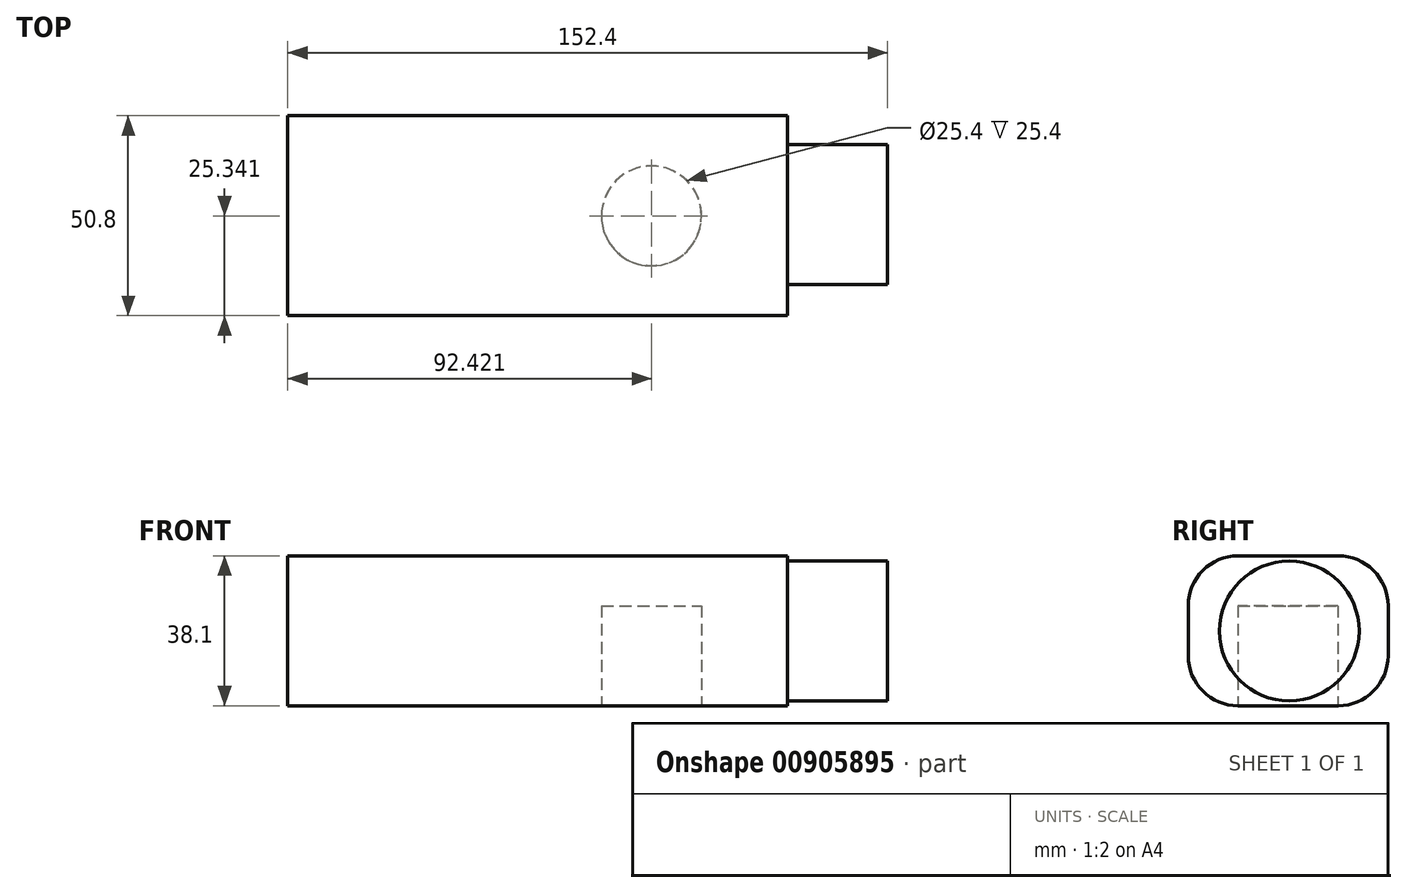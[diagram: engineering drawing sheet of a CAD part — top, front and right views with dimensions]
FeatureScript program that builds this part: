
annotation { "Feature Type Name" : "Feature", "Feature Type Description" : "" }
export const myFeature = defineFeature(function(context is Context, id is Id, definition is map)
    precondition{}
    {
        {
            var Q0;
            Q0=qCreatedBy(makeId("Right.planeOp"),FACE);
            var sketch = newSketch(context, id + "F0", { "sketchPlane" : qUnion([Q0])});
            skLineSegment(sketch, "E0.bottom", {"start": v(-48.2, 38.36) * mm, "end": v(2.6, 38.36) * mm});
            skLineSegment(sketch, "E0.top", {"start": v(-48.2, 0.26) * mm, "end": v(2.6, 0.26) * mm});
            skLineSegment(sketch, "E0.left", {"start": v(-48.2, 38.36) * mm, "end": v(-48.2, 0.26) * mm});
            skLineSegment(sketch, "E0.right", {"start": v(2.6, 38.36) * mm, "end": v(2.6, 0.26) * mm});
            skSolve(sketch);
        }
        {
            var Q0;
            Q0 = qSketchRegion(id + "F0", true);
            extrude(context, id + "F1", {"entities" : qUnion([Q0]), "depth" : 127 * mm, "offsetDistance" : 25.4 * mm});
        }
        {
            var Q0;
            Q0=makeQuery(id+"F1.opExtrude","SWEPT_EDGE",EDGE,{"disambiguationData":[OSD([sQuery(id+"F0.wireOp",EDGE,"E0.bottom"),sQuery(id+"F0.wireOp",EDGE,"E0.left")])]});
            var Q1;
            Q1=makeQuery(id+"F1.opExtrude","SWEPT_EDGE",EDGE,{"disambiguationData":[OSD([sQuery(id+"F0.wireOp",EDGE,"E0.bottom"),sQuery(id+"F0.wireOp",EDGE,"E0.right")])]});
            var Q2;
            Q2=makeQuery(id+"F1.opExtrude","SWEPT_EDGE",EDGE,{"disambiguationData":[OSD([sQuery(id+"F0.wireOp",EDGE,"E0.top"),sQuery(id+"F0.wireOp",EDGE,"E0.left")])]});
            var Q3;
            Q3=makeQuery(id+"F1.opExtrude","SWEPT_EDGE",EDGE,{"disambiguationData":[OSD([sQuery(id+"F0.wireOp",EDGE,"E0.top"),sQuery(id+"F0.wireOp",EDGE,"E0.right")])]});
            fillet(context, id + "F2", {"entities" : qUnion([Q0, Q1, Q2, Q3]), "radius" : 12.7 * mm, "tangentPropagation" : true, "allowEdgeOverflow" : false});
        }
        {
            var Q0;
            Q0=makeQuery(id+"F1.opExtrude","SWEPT_FACE",FACE,{"disambiguationData":[OSD([sQuery(id+"F0.wireOp",EDGE,"E0.top")])]});
            var sketch = newSketch(context, id + "F3", { "sketchPlane" : qUnion([Q0])});
            skCircle(sketch, "E1", {"center": v(92.42, 22.86) * mm, "radius": 12.7 * mm});
            skSolve(sketch);
        }
        {
            var Q0;
            Q0 = qSketchRegion(id + "F3", true);
            extrude(context, id + "F4", {"entities" : qUnion([Q0]), "operationType" : NewBodyOperationType.REMOVE, "oppositeDirection" : true, "depth" : 25.4 * mm, "offsetDistance" : 25.4 * mm});
        }
        {
            var Q0;
            Q0=makeQuery(id+"F1.opExtrude","CAP_FACE",FACE,{"disambiguationData":[OSD([sQuery(id+"F0.wireOp",EDGE,"E0.bottom"),sQuery(id+"F0.wireOp",EDGE,"E0.top"),sQuery(id+"F0.wireOp",EDGE,"E0.left"),sQuery(id+"F0.wireOp",EDGE,"E0.right")])],"isStart":false});
            var sketch = newSketch(context, id + "F5", { "sketchPlane" : qUnion([Q0])});
            skCircle(sketch, "E2", {"center": v(-22.5, 19.24) * mm, "radius": 17.78 * mm});
            skSolve(sketch);
        }
        {
            var Q0;
            Q0 = qSketchRegion(id + "F5", true);
            extrude(context, id + "F6", {"entities" : qUnion([Q0]), "operationType" : NewBodyOperationType.ADD, "depth" : 25.4 * mm, "offsetDistance" : 25.4 * mm});
        }
    });
